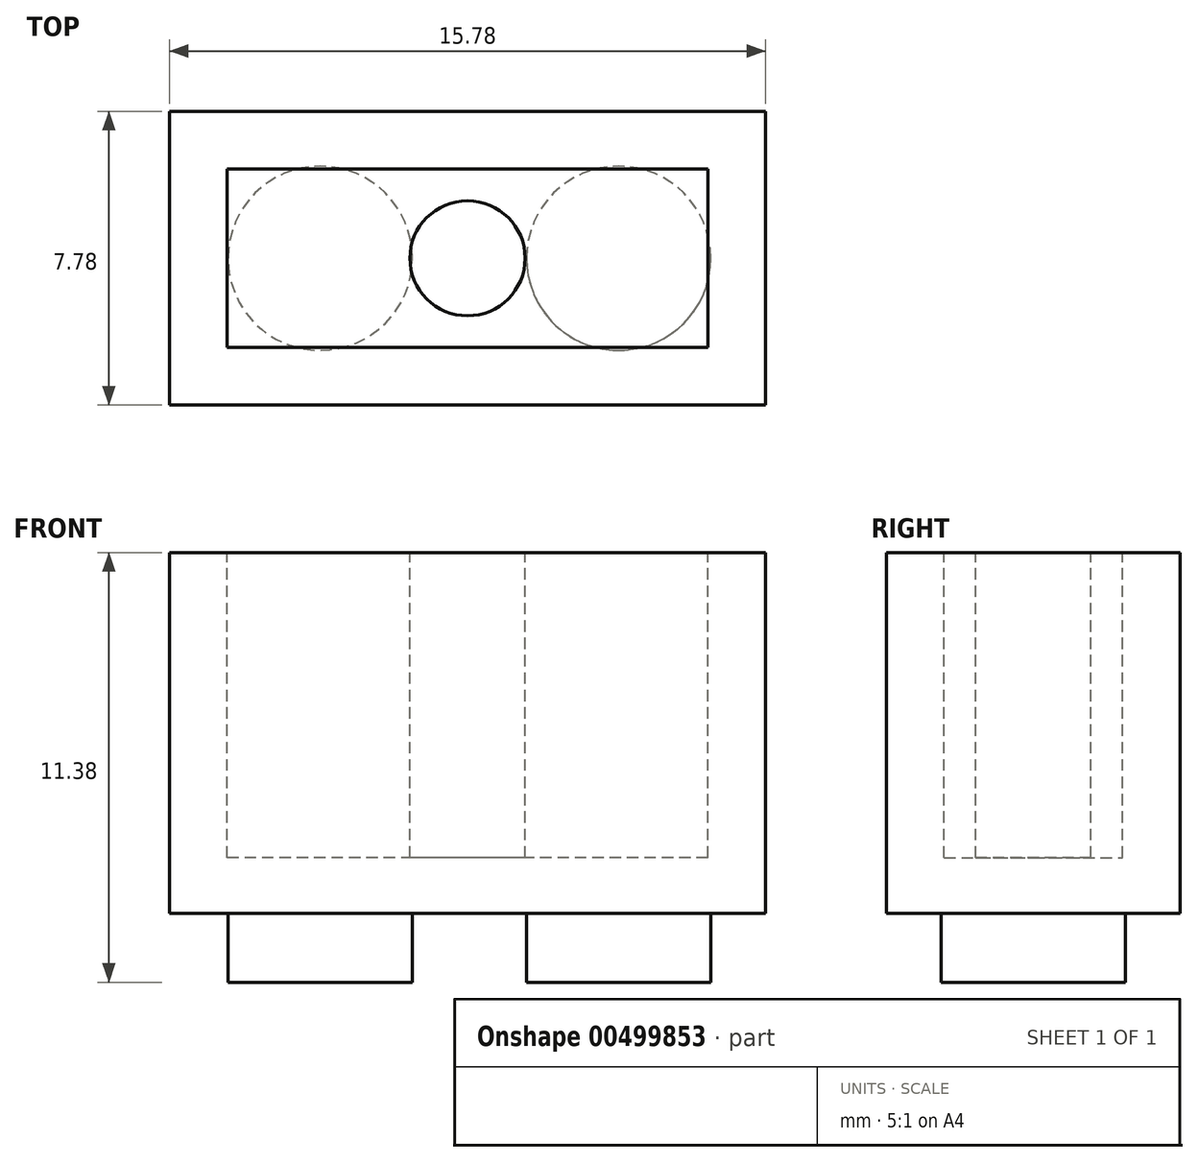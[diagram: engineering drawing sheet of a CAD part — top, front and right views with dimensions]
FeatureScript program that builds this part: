
annotation { "Feature Type Name" : "Feature", "Feature Type Description" : "" }
export const myFeature = defineFeature(function(context is Context, id is Id, definition is map)
    precondition{}
    {
        {
            var Q0;
            Q0=qCreatedBy(makeId("Top.planeOp"),FACE);
            var sketch = newSketch(context, id + "F0", { "sketchPlane" : qUnion([Q0])});
            skLineSegment(sketch, "E0.bottom", {"start": v(7.89, 3.89) * mm, "end": v(-7.89, 3.89) * mm});
            skLineSegment(sketch, "E0.top", {"start": v(7.89, -3.89) * mm, "end": v(-7.89, -3.89) * mm});
            skLineSegment(sketch, "E0.left", {"start": v(7.89, 3.89) * mm, "end": v(7.89, -3.89) * mm});
            skLineSegment(sketch, "E0.right", {"start": v(-7.89, 3.89) * mm, "end": v(-7.89, -3.89) * mm});
            skPoint(sketch, "E0.middle", {"position": v(0, 0) * mm});
            skSolve(sketch);
        }
        {
            var Q0;
            Q0=makeQuery(id+"F0.imprint","IMPRINT",FACE,{"disambiguationData":[TD([[makeQuery(id+"F0.imprint","IMPRINT",EDGE,{"derivedFrom":sQuery(id+"F0.wireOp",EDGE,"E0.bottom")}),1.0]])]});
            extrude(context, id + "F1", {"entities" : qUnion([Q0]), "depth" : 9.55 * mm});
        }
        {
            var Q0;
            Q0=makeQuery(id+"F1.opExtrude","CAP_FACE",FACE,{"disambiguationData":[OSD([sQuery(id+"F0.wireOp",EDGE,"E0.bottom"),sQuery(id+"F0.wireOp",EDGE,"E0.top"),sQuery(id+"F0.wireOp",EDGE,"E0.left"),sQuery(id+"F0.wireOp",EDGE,"E0.right")])],"isStart":false});
            var sketch = newSketch(context, id + "F2", { "sketchPlane" : qUnion([Q0])});
            skCircle(sketch, "E1", {"center": v(0, 0) * mm, "radius": 1.52 * mm});
            skSolve(sketch);
        }
        {
            var Q0;
            Q0=makeQuery(id+"F2.imprint","IMPRINT",FACE,{"disambiguationData":[TD([[makeQuery(id+"F2.imprint","IMPRINT",EDGE,{"derivedFrom":sQuery(id+"F2.wireOp",EDGE,"E1")}),-1.0]])]});
            var sketch = newSketch(context, id + "F3", { "sketchPlane" : qUnion([Q0])});
            skLineSegment(sketch, "E2.bottom", {"start": v(6.36, -2.36) * mm, "end": v(-6.36, -2.36) * mm});
            skLineSegment(sketch, "E2.top", {"start": v(6.36, 2.36) * mm, "end": v(-6.36, 2.36) * mm});
            skLineSegment(sketch, "E2.left", {"start": v(6.36, -2.36) * mm, "end": v(6.36, 2.36) * mm});
            skLineSegment(sketch, "E2.right", {"start": v(-6.36, -2.36) * mm, "end": v(-6.36, 2.36) * mm});
            skPoint(sketch, "E2.middle", {"position": v(0, 0) * mm});
            skSolve(sketch);
        }
        {
            var Q0;
            Q0=makeQuery(id+"F3.imprint","IMPRINT",FACE,{"disambiguationData":[TD([[makeQuery(id+"F3.imprint","IMPRINT",EDGE,{"derivedFrom":sQuery(id+"F3.wireOp",EDGE,"E2.bottom")}),-1.0]])]});
            extrude(context, id + "F4", {"entities" : qUnion([Q0]), "operationType" : NewBodyOperationType.REMOVE, "oppositeDirection" : true, "depth" : 8.08 * mm});
        }
        {
            var Q0;
            Q0=makeQuery(id+"F1.opExtrude","CAP_FACE",FACE,{"disambiguationData":[OSD([sQuery(id+"F0.wireOp",EDGE,"E0.bottom"),sQuery(id+"F0.wireOp",EDGE,"E0.top"),sQuery(id+"F0.wireOp",EDGE,"E0.left"),sQuery(id+"F0.wireOp",EDGE,"E0.right")])],"isStart":true});
            var sketch = newSketch(context, id + "F5", { "sketchPlane" : qUnion([Q0])});
            skCircle(sketch, "E3", {"center": v(-3.9, 0) * mm, "radius": 2.44 * mm});
            skCircle(sketch, "E4.1.0.0", {"center": v(4, 0) * mm, "radius": 2.44 * mm});
            skLineSegment(sketch, "E4.direction1", {"start": v(-3.9, 0) * mm, "end": v(4, 0) * mm, "construction": true});
            skSolve(sketch);
        }
        {
            var Q0;
            Q0=makeQuery(id+"F5.imprint","IMPRINT",FACE,{"disambiguationData":[TD([[makeQuery(id+"F5.imprint","IMPRINT",EDGE,{"derivedFrom":sQuery(id+"F5.wireOp",EDGE,"E3")}),1.0]])]});
            var Q1;
            Q1=makeQuery(id+"F5.imprint","IMPRINT",FACE,{"disambiguationData":[TD([[makeQuery(id+"F5.imprint","IMPRINT",EDGE,{"derivedFrom":sQuery(id+"F5.wireOp",EDGE,"E4.1.0.0")}),1.0]])]});
            extrude(context, id + "F6", {"entities" : qUnion([Q0, Q1]), "operationType" : NewBodyOperationType.ADD, "depth" : 1.83 * mm});
        }
    });
